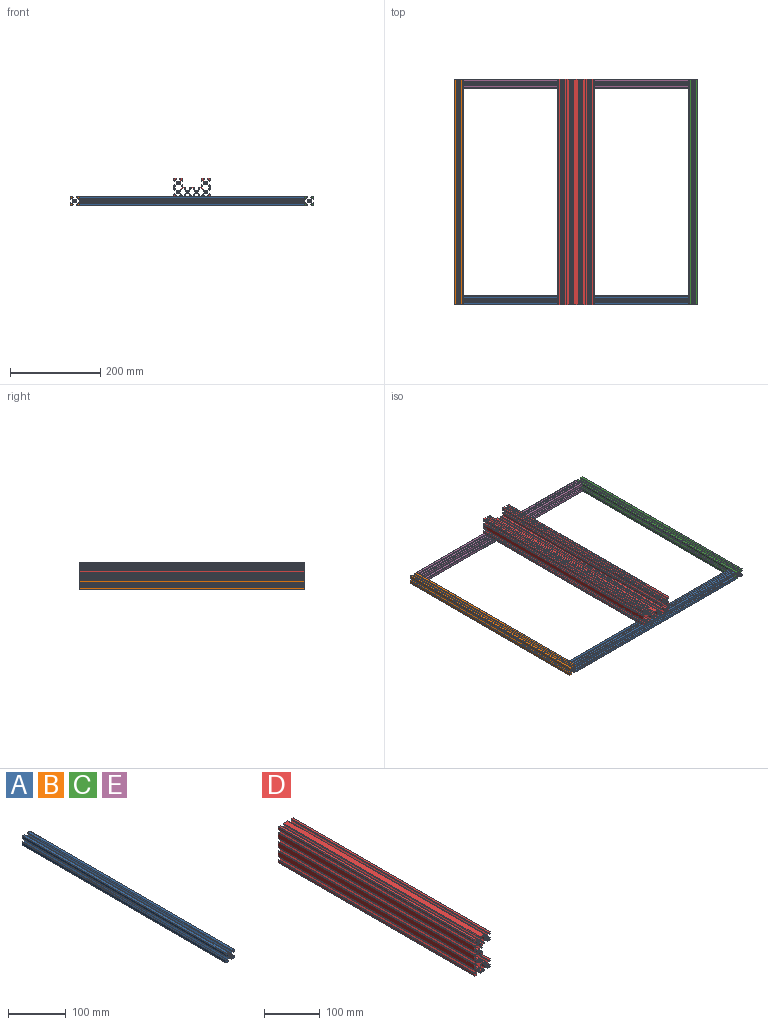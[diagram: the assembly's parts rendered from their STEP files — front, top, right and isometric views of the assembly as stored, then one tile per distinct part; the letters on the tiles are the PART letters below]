
ASSEMBLY  parts=5 mates=4
PART A: 71 faces, bbox 20x500x20 mm
  f0: cylinder r=2.1mm len=500mm, axis (0,1,0), area 6597.3mm2, adj f69,f70
  f1: plane 500x0.21mm, normal (0.71,0,0.71), area 148.5mm2, adj f2,f68,f69,f70
  f2: plane 500x0.21mm, normal (0.71,0,-0.71), area 148.5mm2, adj f1,f3,f69,f70
  f3: plane 500x2.63mm, normal (1,0,0), area 1314.7mm2, adj f2,f4,f69,f70
  f4: plane 500x2.66mm, normal (0.71,0,-0.71), area 1881.4mm2, adj f3,f5,f69,f70
  f5: plane 500x1.64mm, normal (0,0,-1), area 819.7mm2, adj f4,f6,f69,f70
  f6: plane 500x2.38mm, normal (-1,0,0), area 1187.5mm2, adj f5,f7,f69,f70
  f7: plane 500x0.35mm, normal (0,0,-1), area 172.5mm2, adj f6,f8,f69,f70
  f8: plane 500x1.46mm, normal (0.71,0,-0.71), area 1028.8mm2, adj f7,f9,f69,f70
  f9: plane 500x4.92mm, normal (1,0,0), area 2460mm2, adj f8,f10,f69,f70
  f10: cylinder r=0.5mm len=500mm, axis (0,1,0), area 392.7mm2, adj f9,f11,f69,f70
  f11: plane 500x4.92mm, normal (0,0,1), area 2460mm2, adj f10,f12,f69,f70
  f12: plane 500x1.46mm, normal (-0.71,0,0.71), area 1028.8mm2, adj f11,f13,f69,f70
  f13: plane 500x0.35mm, normal (-1,0,0), area 172.5mm2, adj f12,f14,f69,f70
  f14: plane 500x2.38mm, normal (0,0,-1), area 1187.5mm2, adj f13,f15,f69,f70
  f15: plane 500x1.64mm, normal (-1,0,0), area 819.7mm2, adj f14,f16,f69,f70
  f16: plane 500x2.66mm, normal (-0.71,0,0.71), area 1881.4mm2, adj f15,f17,f69,f70
  f17: plane 500x2.63mm, normal (0,0,1), area 1314.7mm2, adj f16,f18,f69,f70
  f18: plane 500x0.21mm, normal (-0.71,0,0.71), area 148.5mm2, adj f17,f19,f69,f70
  f19: plane 500x0.21mm, normal (0.71,0,0.71), area 148.5mm2, adj f18,f20,f69,f70
  f20: plane 500x2.63mm, normal (0,0,1), area 1314.7mm2, adj f19,f21,f69,f70
  f21: plane 500x2.66mm, normal (0.71,0,0.71), area 1881.4mm2, adj f20,f22,f69,f70
  f22: plane 500x1.64mm, normal (1,0,0), area 819.7mm2, adj f21,f23,f69,f70
  f23: plane 500x2.38mm, normal (0,0,-1), area 1187.5mm2, adj f22,f24,f69,f70
  f24: plane 500x0.35mm, normal (1,0,0), area 172.5mm2, adj f23,f25,f69,f70
  f25: plane 500x1.46mm, normal (0.71,0,0.71), area 1028.8mm2, adj f24,f26,f69,f70
  f26: plane 500x4.92mm, normal (0,0,1), area 2460mm2, adj f25,f27,f69,f70
  f27: cylinder r=0.5mm len=500mm, axis (0,1,0), area 392.7mm2, adj f26,f28,f69,f70
  f28: plane 500x4.92mm, normal (-1,0,0), area 2460mm2, adj f27,f29,f69,f70
  f29: plane 500x1.46mm, normal (-0.71,0,-0.71), area 1028.8mm2, adj f28,f30,f69,f70
  f30: plane 500x0.35mm, normal (0,0,-1), area 172.5mm2, adj f29,f31,f69,f70
  f31: plane 500x2.38mm, normal (1,0,0), area 1187.5mm2, adj f30,f32,f69,f70
  f32: plane 500x1.64mm, normal (0,0,-1), area 819.7mm2, adj f31,f33,f69,f70
  f33: plane 500x2.66mm, normal (-0.71,0,-0.71), area 1881.4mm2, adj f32,f34,f69,f70
  f34: plane 500x2.63mm, normal (-1,0,0), area 1314.7mm2, adj f33,f35,f69,f70
  f35: plane 500x0.21mm, normal (-0.71,0,-0.71), area 148.5mm2, adj f34,f36,f69,f70
  f36: plane 500x0.21mm, normal (-0.71,0,0.71), area 148.5mm2, adj f35,f37,f69,f70
  f37: plane 500x2.63mm, normal (-1,0,0), area 1314.7mm2, adj f36,f38,f69,f70
  f38: plane 500x2.66mm, normal (-0.71,0,0.71), area 1881.4mm2, adj f37,f39,f69,f70
  f39: plane 500x1.64mm, normal (0,0,1), area 819.7mm2, adj f38,f40,f69,f70
  f40: plane 500x2.38mm, normal (1,0,0), area 1187.5mm2, adj f39,f41,f69,f70
  f41: plane 500x0.35mm, normal (0,0,1), area 172.5mm2, adj f40,f42,f69,f70
  f42: plane 500x1.46mm, normal (-0.71,0,0.71), area 1028.8mm2, adj f41,f43,f69,f70
  f43: plane 500x4.92mm, normal (-1,0,0), area 2460mm2, adj f42,f44,f69,f70
  f44: cylinder r=0.5mm len=500mm, axis (0,1,0), area 392.7mm2, adj f43,f45,f69,f70
  f45: plane 500x4.92mm, normal (0,0,-1), area 2460mm2, adj f44,f46,f69,f70
  f46: plane 500x1.46mm, normal (0.71,0,-0.71), area 1028.8mm2, adj f45,f47,f69,f70
  f47: plane 500x0.35mm, normal (1,0,0), area 172.5mm2, adj f46,f48,f69,f70
  f48: plane 500x2.38mm, normal (0,0,1), area 1187.5mm2, adj f47,f49,f69,f70
  f49: plane 500x1.64mm, normal (1,0,0), area 819.7mm2, adj f48,f50,f69,f70
  f50: plane 500x2.66mm, normal (0.71,0,-0.71), area 1881.4mm2, adj f49,f51,f69,f70
  f51: plane 500x2.63mm, normal (0,0,-1), area 1314.7mm2, adj f50,f52,f69,f70
  f52: plane 500x0.21mm, normal (0.71,0,-0.71), area 148.5mm2, adj f51,f53,f69,f70
  f53: plane 500x0.21mm, normal (-0.71,0,-0.71), area 148.5mm2, adj f52,f54,f69,f70
  f54: plane 500x2.63mm, normal (0,0,-1), area 1314.7mm2, adj f53,f55,f69,f70
  f55: plane 500x2.66mm, normal (-0.71,0,-0.71), area 1881.4mm2, adj f54,f56,f69,f70
  f56: plane 500x1.64mm, normal (-1,0,0), area 819.7mm2, adj f55,f57,f69,f70
  f57: plane 500x2.38mm, normal (0,0,1), area 1187.5mm2, adj f56,f58,f69,f70
  f58: plane 500x0.35mm, normal (-1,0,0), area 172.5mm2, adj f57,f59,f69,f70
  f59: plane 500x1.46mm, normal (-0.71,0,-0.71), area 1028.8mm2, adj f58,f60,f69,f70
  f60: plane 500x4.92mm, normal (0,0,-1), area 2460mm2, adj f59,f61,f69,f70
  f61: cylinder r=0.5mm len=500mm, axis (0,1,0), area 392.7mm2, adj f60,f62,f69,f70
  f62: plane 500x4.92mm, normal (1,0,0), area 2460mm2, adj f61,f63,f69,f70
  f63: plane 500x1.46mm, normal (0.71,0,0.71), area 1028.8mm2, adj f62,f64,f69,f70
  f64: plane 500x0.35mm, normal (0,0,1), area 172.5mm2, adj f63,f65,f69,f70
  f65: plane 500x2.38mm, normal (-1,0,0), area 1187.5mm2, adj f64,f66,f69,f70
  f66: plane 500x1.64mm, normal (0,0,1), area 819.7mm2, adj f65,f67,f69,f70
  f67: plane 500x2.66mm, normal (0.71,0,0.71), area 1881.4mm2, adj f66,f68,f69,f70
  f68: plane 500x2.63mm, normal (1,0,0), area 1314.7mm2, adj f1,f67,f69,f70
  f69: plane 20x20mm, normal (0,-1,0), area 171.4mm2, adj f0,f1,f2,f3,f4,f5,f6,f7
  f70: plane 20x20mm, normal (0,1,0), area 171.4mm2, adj f0,f1,f2,f3,f4,f5,f6,f7
PART B: same geometry as A
PART C: same geometry as A
PART D: 288 faces, bbox 40x500x80 mm
  f0: cylinder r=2.3mm len=500mm, axis (0,1,0), area 7225.7mm2, adj f286,f287
  f1: cylinder r=2.3mm len=500mm, axis (0,1,0), area 7225.7mm2, adj f286,f287
  f2: cylinder r=2.3mm len=500mm, axis (0,1,0), area 7225.7mm2, adj f286,f287
  f3: cylinder r=2.3mm len=500mm, axis (0,1,0), area 7225.7mm2, adj f286,f287
  f4: cylinder r=2.3mm len=500mm, axis (0,1,0), area 7225.7mm2, adj f286,f287
  f5: cylinder r=2.3mm len=500mm, axis (0,1,0), area 7225.7mm2, adj f286,f287
  f6: plane 500x0.21mm, normal (0.71,0,0.71), area 148.5mm2, adj f7,f280,f286,f287
  f7: plane 500x0.21mm, normal (0.71,0,-0.71), area 148.5mm2, adj f6,f8,f286,f287
  f8: plane 500x2.63mm, normal (1,0,0), area 1314.7mm2, adj f7,f9,f286,f287
  f9: plane 500x2.66mm, normal (0.71,0,-0.71), area 1881.4mm2, adj f8,f10,f286,f287
  f10: plane 500x1.64mm, normal (0,0,-1), area 819.7mm2, adj f9,f11,f286,f287
  f11: plane 500x2.11mm, normal (-1,0,0), area 1052.5mm2, adj f10,f12,f286,f287
  f12: plane 500x0.62mm, normal (0,0,-1), area 307.5mm2, adj f11,f13,f286,f287
  f13: plane 500x1.19mm, normal (0.71,0,-0.71), area 837.9mm2, adj f12,f14,f286,f287
  f14: plane 500x3.92mm, normal (1,0,0), area 1960mm2, adj f13,f15,f286,f287
  f15: cylinder r=1.5mm len=500mm, axis (0,1,0), area 1178.1mm2, adj f14,f16,f286,f287
  f16: plane 500x3.92mm, normal (0,0,1), area 1960mm2, adj f15,f17,f286,f287
  f17: plane 500x1.19mm, normal (-0.71,0,0.71), area 837.9mm2, adj f16,f18,f286,f287
  f18: plane 500x0.62mm, normal (-1,0,0), area 307.5mm2, adj f17,f19,f286,f287
  f19: plane 500x2.11mm, normal (0,0,-1), area 1052.5mm2, adj f18,f20,f286,f287
  f20: plane 500x1.64mm, normal (-1,0,0), area 819.7mm2, adj f19,f21,f286,f287
  f21: plane 500x2.66mm, normal (-0.71,0,0.71), area 1881.4mm2, adj f20,f22,f286,f287
  f22: plane 500x2.63mm, normal (0,0,1), area 1314.7mm2, adj f21,f23,f286,f287
  f23: plane 500x0.21mm, normal (-0.71,0,0.71), area 148.5mm2, adj f22,f24,f286,f287
  f24: plane 500x0.21mm, normal (0.71,0,0.71), area 148.5mm2, adj f23,f25,f286,f287
  f25: plane 500x2.63mm, normal (0,0,1), area 1314.7mm2, adj f24,f26,f286,f287
  f26: plane 500x2.66mm, normal (0.71,0,0.71), area 1881.4mm2, adj f25,f27,f286,f287
  f27: plane 500x1.64mm, normal (1,0,0), area 819.7mm2, adj f26,f28,f286,f287
  f28: plane 500x2.11mm, normal (0,0,-1), area 1052.5mm2, adj f27,f29,f286,f287
  f29: plane 500x0.62mm, normal (1,0,0), area 307.5mm2, adj f28,f30,f286,f287
  f30: plane 500x1.19mm, normal (0.71,0,0.71), area 837.9mm2, adj f29,f31,f286,f287
  f31: plane 500x10.84mm, normal (0,0,1), area 5420mm2, adj f30,f32,f286,f287
  f32: plane 500x1.19mm, normal (-0.71,0,0.71), area 837.9mm2, adj f31,f33,f286,f287
  f33: plane 500x0.62mm, normal (-1,0,0), area 307.5mm2, adj f32,f34,f286,f287
  f34: plane 500x2.11mm, normal (0,0,-1), area 1052.5mm2, adj f33,f35,f286,f287
  f35: plane 500x1.64mm, normal (-1,0,0), area 819.7mm2, adj f34,f36,f286,f287
  f36: plane 500x2.66mm, normal (-0.71,0,0.71), area 1881.4mm2, adj f35,f37,f286,f287
  f37: plane 500x2.63mm, normal (0,0,1), area 1314.7mm2, adj f36,f38,f286,f287
  f38: plane 500x0.21mm, normal (-0.71,0,0.71), area 148.5mm2, adj f37,f39,f286,f287
  f39: plane 500x0.21mm, normal (0.71,0,0.71), area 148.5mm2, adj f38,f40,f286,f287
  f40: plane 500x2.63mm, normal (0,0,1), area 1314.7mm2, adj f39,f41,f286,f287
  f41: plane 500x2.66mm, normal (0.71,0,0.71), area 1881.4mm2, adj f40,f42,f286,f287
  f42: plane 500x1.64mm, normal (1,0,0), area 819.7mm2, adj f41,f43,f286,f287
  f43: plane 500x2.11mm, normal (0,0,-1), area 1052.5mm2, adj f42,f44,f286,f287
  f44: plane 500x0.62mm, normal (1,0,0), area 307.5mm2, adj f43,f45,f286,f287
  f45: plane 500x1.19mm, normal (0.71,0,0.71), area 837.9mm2, adj f44,f46,f286,f287
  f46: plane 500x3.92mm, normal (0,0,1), area 1960mm2, adj f45,f47,f286,f287
  f47: cylinder r=1.5mm len=500mm, axis (0,1,0), area 1178.1mm2, adj f46,f48,f286,f287
  f48: plane 500x3.92mm, normal (-1,0,0), area 1960mm2, adj f47,f49,f286,f287
  f49: plane 500x1.19mm, normal (-0.71,0,-0.71), area 837.9mm2, adj f48,f50,f286,f287
  f50: plane 500x0.62mm, normal (0,0,-1), area 307.5mm2, adj f49,f51,f286,f287
  f51: plane 500x2.11mm, normal (1,0,0), area 1052.5mm2, adj f50,f52,f286,f287
  f52: plane 500x1.64mm, normal (0,0,-1), area 819.7mm2, adj f51,f53,f286,f287
  f53: plane 500x2.66mm, normal (-0.71,0,-0.71), area 1881.4mm2, adj f52,f54,f286,f287
  f54: plane 500x2.63mm, normal (-1,0,0), area 1314.7mm2, adj f53,f55,f286,f287
  f55: plane 500x0.21mm, normal (-0.71,0,-0.71), area 148.5mm2, adj f54,f56,f286,f287
  f56: plane 500x0.21mm, normal (-0.71,0,0.71), area 148.5mm2, adj f55,f57,f286,f287
  f57: plane 500x2.63mm, normal (-1,0,0), area 1314.7mm2, adj f56,f58,f286,f287
  f58: plane 500x2.66mm, normal (-0.71,0,0.71), area 1881.4mm2, adj f57,f59,f286,f287
  f59: plane 500x1.64mm, normal (0,0,1), area 819.7mm2, adj f58,f60,f286,f287
  f60: plane 500x2.11mm, normal (1,0,0), area 1052.5mm2, adj f59,f61,f286,f287
  f61: plane 500x0.62mm, normal (0,0,1), area 307.5mm2, adj f60,f62,f286,f287
  f62: plane 500x1.19mm, normal (-0.71,0,0.71), area 837.9mm2, adj f61,f63,f286,f287
  f63: plane 500x10.84mm, normal (-1,0,0), area 5420mm2, adj f62,f64,f286,f287
  f64: plane 500x1.19mm, normal (-0.71,0,-0.71), area 837.9mm2, adj f63,f65,f286,f287
  f65: plane 500x0.62mm, normal (0,0,-1), area 307.5mm2, adj f64,f66,f286,f287
  f66: plane 500x2.11mm, normal (1,0,0), area 1052.5mm2, adj f65,f67,f286,f287
  f67: plane 500x1.64mm, normal (0,0,-1), area 819.7mm2, adj f66,f68,f286,f287
  f68: plane 500x2.66mm, normal (-0.71,0,-0.71), area 1881.4mm2, adj f67,f69,f286,f287
  f69: plane 500x2.63mm, normal (-1,0,0), area 1314.7mm2, adj f68,f70,f286,f287
  f70: plane 500x0.21mm, normal (-0.71,0,-0.71), area 148.5mm2, adj f69,f71,f286,f287
  f71: plane 500x0.21mm, normal (-0.71,0,0.71), area 148.5mm2, adj f70,f72,f286,f287
  f72: plane 500x2.63mm, normal (-1,0,0), area 1314.7mm2, adj f71,f73,f286,f287
  f73: plane 500x2.66mm, normal (-0.71,0,0.71), area 1881.4mm2, adj f72,f74,f286,f287
  f74: plane 500x1.64mm, normal (0,0,1), area 819.7mm2, adj f73,f75,f286,f287
  f75: plane 500x2.11mm, normal (1,0,0), area 1052.5mm2, adj f74,f76,f286,f287
  f76: plane 500x0.62mm, normal (0,0,1), area 307.5mm2, adj f75,f77,f286,f287
  f77: plane 500x1.19mm, normal (-0.71,0,0.71), area 837.9mm2, adj f76,f78,f286,f287
  f78: plane 500x10.84mm, normal (-1,0,0), area 5420mm2, adj f77,f79,f286,f287
  f79: plane 500x1.19mm, normal (-0.71,0,-0.71), area 837.9mm2, adj f78,f80,f286,f287
  f80: plane 500x0.62mm, normal (0,0,-1), area 307.5mm2, adj f79,f81,f286,f287
  f81: plane 500x2.11mm, normal (1,0,0), area 1052.5mm2, adj f80,f82,f286,f287
  f82: plane 500x1.64mm, normal (0,0,-1), area 819.7mm2, adj f81,f83,f286,f287
  f83: plane 500x2.66mm, normal (-0.71,0,-0.71), area 1881.4mm2, adj f82,f84,f286,f287
  f84: plane 500x2.63mm, normal (-1,0,0), area 1314.7mm2, adj f83,f85,f286,f287
  f85: plane 500x0.21mm, normal (-0.71,0,-0.71), area 148.5mm2, adj f84,f86,f286,f287
  f86: plane 500x0.21mm, normal (-0.71,0,0.71), area 148.5mm2, adj f85,f87,f286,f287
  f87: plane 500x2.63mm, normal (-1,0,0), area 1314.7mm2, adj f86,f88,f286,f287
  f88: plane 500x2.66mm, normal (-0.71,0,0.71), area 1881.4mm2, adj f87,f89,f286,f287
  f89: plane 500x1.64mm, normal (0,0,1), area 819.7mm2, adj f88,f90,f286,f287
  f90: plane 500x2.11mm, normal (1,0,0), area 1052.5mm2, adj f89,f91,f286,f287
  f91: plane 500x0.62mm, normal (0,0,1), area 307.5mm2, adj f90,f92,f286,f287
  f92: plane 500x1.19mm, normal (-0.71,0,0.71), area 837.9mm2, adj f91,f93,f286,f287
  f93: plane 500x10.84mm, normal (-1,0,0), area 5420mm2, adj f92,f94,f286,f287
  f94: plane 500x1.19mm, normal (-0.71,0,-0.71), area 837.9mm2, adj f93,f95,f286,f287
  f95: plane 500x0.62mm, normal (0,0,-1), area 307.5mm2, adj f94,f96,f286,f287
  f96: plane 500x2.11mm, normal (1,0,0), area 1052.5mm2, adj f95,f97,f286,f287
  f97: plane 500x1.64mm, normal (0,0,-1), area 819.7mm2, adj f96,f98,f286,f287
  f98: plane 500x2.66mm, normal (-0.71,0,-0.71), area 1881.4mm2, adj f97,f99,f286,f287
  f99: plane 500x2.63mm, normal (-1,0,0), area 1314.7mm2, adj f98,f100,f286,f287
  f100: plane 500x0.21mm, normal (-0.71,0,-0.71), area 148.5mm2, adj f99,f101,f286,f287
  f101: plane 500x0.21mm, normal (-0.71,0,0.71), area 148.5mm2, adj f100,f102,f286,f287
  f102: plane 500x2.63mm, normal (-1,0,0), area 1314.7mm2, adj f101,f103,f286,f287
  f103: plane 500x2.66mm, normal (-0.71,0,0.71), area 1881.4mm2, adj f102,f104,f286,f287
  f104: plane 500x1.64mm, normal (0,0,1), area 819.7mm2, adj f103,f105,f286,f287
  f105: plane 500x2.11mm, normal (1,0,0), area 1052.5mm2, adj f104,f106,f286,f287
  f106: plane 500x0.62mm, normal (0,0,1), area 307.5mm2, adj f105,f107,f286,f287
  f107: plane 500x1.19mm, normal (-0.71,0,0.71), area 837.9mm2, adj f106,f108,f286,f287
  f108: plane 500x3.92mm, normal (-1,0,0), area 1960mm2, adj f107,f109,f286,f287
  f109: cylinder r=1.5mm len=500mm, axis (0,1,0), area 1178.1mm2, adj f108,f110,f286,f287
  f110: plane 500x3.92mm, normal (0,0,-1), area 1960mm2, adj f109,f111,f286,f287
  f111: plane 500x1.19mm, normal (0.71,0,-0.71), area 837.9mm2, adj f110,f112,f286,f287
  f112: plane 500x0.62mm, normal (1,0,0), area 307.5mm2, adj f111,f113,f286,f287
  f113: plane 500x2.11mm, normal (0,0,1), area 1052.5mm2, adj f112,f114,f286,f287
  f114: plane 500x1.64mm, normal (1,0,0), area 819.7mm2, adj f113,f115,f286,f287
  f115: plane 500x2.66mm, normal (0.71,0,-0.71), area 1881.4mm2, adj f114,f116,f286,f287
  f116: plane 500x2.63mm, normal (0,0,-1), area 1314.7mm2, adj f115,f117,f286,f287
  f117: plane 500x0.21mm, normal (0.71,0,-0.71), area 148.5mm2, adj f116,f118,f286,f287
  f118: plane 500x0.21mm, normal (-0.71,0,-0.71), area 148.5mm2, adj f117,f119,f286,f287
  f119: plane 500x2.63mm, normal (0,0,-1), area 1314.7mm2, adj f118,f120,f286,f287
  f120: plane 500x2.66mm, normal (-0.71,0,-0.71), area 1881.4mm2, adj f119,f121,f286,f287
  f121: plane 500x1.64mm, normal (-1,0,0), area 819.7mm2, adj f120,f122,f286,f287
  f122: plane 500x2.11mm, normal (0,0,1), area 1052.5mm2, adj f121,f123,f286,f287
  f123: plane 500x0.62mm, normal (-1,0,0), area 307.5mm2, adj f122,f124,f286,f287
  f124: plane 500x1.19mm, normal (-0.71,0,-0.71), area 837.9mm2, adj f123,f125,f286,f287
  f125: plane 500x10.84mm, normal (0,0,-1), area 5420mm2, adj f124,f126,f286,f287
  f126: plane 500x1.19mm, normal (0.71,0,-0.71), area 837.9mm2, adj f125,f127,f286,f287
  f127: plane 500x0.62mm, normal (1,0,0), area 307.5mm2, adj f126,f128,f286,f287
  f128: plane 500x2.11mm, normal (0,0,1), area 1052.5mm2, adj f127,f129,f286,f287
  f129: plane 500x1.64mm, normal (1,0,0), area 819.7mm2, adj f128,f130,f286,f287
  f130: plane 500x2.66mm, normal (0.71,0,-0.71), area 1881.4mm2, adj f129,f131,f286,f287
  f131: plane 500x2.63mm, normal (0,0,-1), area 1314.7mm2, adj f130,f132,f286,f287
  f132: plane 500x0.21mm, normal (0.71,0,-0.71), area 148.5mm2, adj f131,f133,f286,f287
  f133: plane 500x0.21mm, normal (-0.71,0,-0.71), area 148.5mm2, adj f132,f134,f286,f287
  f134: plane 500x2.63mm, normal (0,0,-1), area 1314.7mm2, adj f133,f135,f286,f287
  f135: plane 500x2.66mm, normal (-0.71,0,-0.71), area 1881.4mm2, adj f134,f136,f286,f287
  f136: plane 500x1.64mm, normal (-1,0,0), area 819.7mm2, adj f135,f137,f286,f287
  f137: plane 500x2.11mm, normal (0,0,1), area 1052.5mm2, adj f136,f138,f286,f287
  f138: plane 500x0.62mm, normal (-1,0,0), area 307.5mm2, adj f137,f139,f286,f287
  f139: plane 500x1.19mm, normal (-0.71,0,-0.71), area 837.9mm2, adj f138,f140,f286,f287
  f140: plane 500x3.92mm, normal (0,0,-1), area 1960mm2, adj f139,f141,f286,f287
  f141: cylinder r=1.5mm len=500mm, axis (0,1,0), area 1178.1mm2, adj f140,f142,f286,f287
  f142: plane 500x3.92mm, normal (1,0,0), area 1960mm2, adj f141,f143,f286,f287
  f143: plane 500x1.19mm, normal (0.71,0,0.71), area 837.9mm2, adj f142,f144,f286,f287
  f144: plane 500x0.62mm, normal (0,0,1), area 307.5mm2, adj f143,f145,f286,f287
  f145: plane 500x2.11mm, normal (-1,0,0), area 1052.5mm2, adj f144,f146,f286,f287
  f146: plane 500x1.64mm, normal (0,0,1), area 819.7mm2, adj f145,f147,f286,f287
  f147: plane 500x2.66mm, normal (0.71,0,0.71), area 1881.4mm2, adj f146,f148,f286,f287
  f148: plane 500x2.63mm, normal (1,0,0), area 1314.7mm2, adj f147,f149,f286,f287
  f149: plane 500x0.21mm, normal (0.71,0,0.71), area 148.5mm2, adj f148,f150,f286,f287
  f150: plane 500x0.21mm, normal (0.71,0,-0.71), area 148.5mm2, adj f149,f151,f286,f287
  f151: plane 500x2.63mm, normal (1,0,0), area 1314.7mm2, adj f150,f152,f286,f287
  f152: plane 500x2.66mm, normal (0.71,0,-0.71), area 1881.4mm2, adj f151,f153,f286,f287
  f153: plane 500x1.64mm, normal (0,0,-1), area 819.7mm2, adj f152,f154,f286,f287
  f154: plane 500x2.11mm, normal (-1,0,0), area 1052.5mm2, adj f153,f155,f286,f287
  f155: plane 500x0.62mm, normal (0,0,-1), area 307.5mm2, adj f154,f156,f286,f287
  f156: plane 500x1.19mm, normal (0.71,0,-0.71), area 837.9mm2, adj f155,f157,f286,f287
  f157: plane 500x3.92mm, normal (1,0,0), area 1960mm2, adj f156,f158,f286,f287
  f158: cylinder r=1.5mm len=500mm, axis (0,1,0), area 1178.1mm2, adj f157,f159,f286,f287
  f159: plane 500x3.92mm, normal (0,0,1), area 1960mm2, adj f158,f160,f286,f287
  f160: plane 500x1.19mm, normal (-0.71,0,0.71), area 837.9mm2, adj f159,f161,f286,f287
  f161: plane 500x0.62mm, normal (-1,0,0), area 307.5mm2, adj f160,f162,f286,f287
  f162: plane 500x2.11mm, normal (0,0,-1), area 1052.5mm2, adj f161,f163,f286,f287
  f163: plane 500x1.64mm, normal (-1,0,0), area 819.7mm2, adj f162,f164,f286,f287
  f164: plane 500x2.66mm, normal (-0.71,0,0.71), area 1881.4mm2, adj f163,f165,f286,f287
  f165: plane 500x2.63mm, normal (0,0,1), area 1314.7mm2, adj f164,f166,f286,f287
  f166: plane 500x0.21mm, normal (-0.71,0,0.71), area 148.5mm2, adj f165,f167,f286,f287
  f167: plane 500x0.21mm, normal (0.71,0,0.71), area 148.5mm2, adj f166,f168,f286,f287
  f168: plane 500x2.63mm, normal (0,0,1), area 1314.7mm2, adj f167,f169,f286,f287
  f169: plane 500x2.66mm, normal (0.71,0,0.71), area 1881.4mm2, adj f168,f170,f286,f287
  f170: plane 500x1.64mm, normal (1,0,0), area 819.7mm2, adj f169,f171,f286,f287
  f171: plane 500x2.11mm, normal (0,0,-1), area 1052.5mm2, adj f170,f172,f286,f287
  f172: plane 500x0.62mm, normal (1,0,0), area 307.5mm2, adj f171,f173,f286,f287
  f173: plane 500x1.19mm, normal (0.71,0,0.71), area 837.9mm2, adj f172,f174,f286,f287
  f174: plane 500x5.42mm, normal (0,0,1), area 2710mm2, adj f173,f175,f286,f287
  f175: plane 500x5.42mm, normal (1,0,0), area 2710mm2, adj f174,f176,f286,f287
  f176: plane 500x1.19mm, normal (0.71,0,0.71), area 837.9mm2, adj f175,f177,f286,f287
  f177: plane 500x0.62mm, normal (0,0,1), area 307.5mm2, adj f176,f178,f286,f287
  f178: plane 500x2.11mm, normal (-1,0,0), area 1052.5mm2, adj f177,f179,f286,f287
  f179: plane 500x1.64mm, normal (0,0,1), area 819.7mm2, adj f178,f180,f286,f287
  f180: plane 500x2.66mm, normal (0.71,0,0.71), area 1881.4mm2, adj f179,f181,f286,f287
  f181: plane 500x2.63mm, normal (1,0,0), area 1314.7mm2, adj f180,f182,f286,f287
  f182: plane 500x0.21mm, normal (0.71,0,0.71), area 148.5mm2, adj f181,f183,f286,f287
  f183: plane 500x0.21mm, normal (0.71,0,-0.71), area 148.5mm2, adj f182,f184,f286,f287
  f184: plane 500x2.63mm, normal (1,0,0), area 1314.7mm2, adj f183,f185,f286,f287
  f185: plane 500x2.66mm, normal (0.71,0,-0.71), area 1881.4mm2, adj f184,f186,f286,f287
  f186: plane 500x1.64mm, normal (0,0,-1), area 819.7mm2, adj f185,f187,f286,f287
  f187: plane 500x2.11mm, normal (-1,0,0), area 1052.5mm2, adj f186,f188,f286,f287
  f188: plane 500x0.62mm, normal (0,0,-1), area 307.5mm2, adj f187,f189,f286,f287
  f189: plane 500x1.19mm, normal (0.71,0,-0.71), area 837.9mm2, adj f188,f190,f286,f287
  f190: plane 500x10.84mm, normal (1,0,0), area 5420mm2, adj f189,f191,f286,f287
  f191: plane 500x1.19mm, normal (0.71,0,0.71), area 837.9mm2, adj f190,f192,f286,f287
  f192: plane 500x0.62mm, normal (0,0,1), area 307.5mm2, adj f191,f193,f286,f287
  f193: plane 500x2.11mm, normal (-1,0,0), area 1052.5mm2, adj f192,f194,f286,f287
  f194: plane 500x1.64mm, normal (0,0,1), area 819.7mm2, adj f193,f195,f286,f287
  f195: plane 500x2.66mm, normal (0.71,0,0.71), area 1881.4mm2, adj f194,f196,f286,f287
  f196: plane 500x2.63mm, normal (1,0,0), area 1314.7mm2, adj f195,f197,f286,f287
  f197: plane 500x0.21mm, normal (0.71,0,0.71), area 148.5mm2, adj f196,f198,f286,f287
  f198: plane 500x0.21mm, normal (0.71,0,-0.71), area 148.5mm2, adj f197,f199,f286,f287
  f199: plane 500x2.63mm, normal (1,0,0), area 1314.7mm2, adj f198,f200,f286,f287
  f200: plane 500x2.66mm, normal (0.71,0,-0.71), area 1881.4mm2, adj f199,f201,f286,f287
  f201: plane 500x1.64mm, normal (0,0,-1), area 819.7mm2, adj f200,f202,f286,f287
  f202: plane 500x2.11mm, normal (-1,0,0), area 1052.5mm2, adj f201,f203,f286,f287
  f203: plane 500x0.62mm, normal (0,0,-1), area 307.5mm2, adj f202,f204,f286,f287
  f204: plane 500x1.19mm, normal (0.71,0,-0.71), area 837.9mm2, adj f203,f205,f286,f287
  f205: plane 500x5.42mm, normal (1,0,0), area 2710mm2, adj f204,f206,f286,f287
  f206: plane 500x5.42mm, normal (0,0,-1), area 2710mm2, adj f205,f207,f286,f287
  f207: plane 500x1.19mm, normal (0.71,0,-0.71), area 837.9mm2, adj f206,f208,f286,f287
  f208: plane 500x0.62mm, normal (1,0,0), area 307.5mm2, adj f207,f209,f286,f287
  f209: plane 500x2.11mm, normal (0,0,1), area 1052.5mm2, adj f208,f210,f286,f287
  f210: plane 500x1.64mm, normal (1,0,0), area 819.7mm2, adj f209,f211,f286,f287
  f211: plane 500x2.66mm, normal (0.71,0,-0.71), area 1881.4mm2, adj f210,f212,f286,f287
  f212: plane 500x2.63mm, normal (0,0,-1), area 1314.7mm2, adj f211,f213,f286,f287
  f213: plane 500x0.21mm, normal (0.71,0,-0.71), area 148.5mm2, adj f212,f214,f286,f287
  f214: plane 500x0.21mm, normal (-0.71,0,-0.71), area 148.5mm2, adj f213,f215,f286,f287
  f215: plane 500x2.63mm, normal (0,0,-1), area 1314.7mm2, adj f214,f216,f286,f287
  f216: plane 500x2.66mm, normal (-0.71,0,-0.71), area 1881.4mm2, adj f215,f217,f286,f287
  f217: plane 500x1.64mm, normal (-1,0,0), area 819.7mm2, adj f216,f218,f286,f287
  f218: plane 500x2.11mm, normal (0,0,1), area 1052.5mm2, adj f217,f219,f286,f287
  f219: plane 500x0.62mm, normal (-1,0,0), area 307.5mm2, adj f218,f220,f286,f287
  f220: plane 500x1.19mm, normal (-0.71,0,-0.71), area 837.9mm2, adj f219,f221,f286,f287
  f221: plane 500x3.92mm, normal (0,0,-1), area 1960mm2, adj f220,f222,f286,f287
  f222: cylinder r=1.5mm len=500mm, axis (0,1,0), area 1178.1mm2, adj f221,f223,f286,f287
  f223: plane 500x3.92mm, normal (1,0,0), area 1960mm2, adj f222,f224,f286,f287
  f224: plane 500x1.19mm, normal (0.71,0,0.71), area 837.9mm2, adj f223,f225,f286,f287
  f225: plane 500x0.62mm, normal (0,0,1), area 307.5mm2, adj f224,f226,f286,f287
  f226: plane 500x2.11mm, normal (-1,0,0), area 1052.5mm2, adj f225,f227,f286,f287
  f227: plane 500x1.64mm, normal (0,0,1), area 819.7mm2, adj f226,f228,f286,f287
  f228: plane 500x2.66mm, normal (0.71,0,0.71), area 1881.4mm2, adj f227,f280,f286,f287
  f229: plane 500x1.96mm, normal (0,0,1), area 980.3mm2, adj f230,f281,f286,f287
  f230: plane 500x5.4mm, normal (1,0,0), area 2700mm2, adj f229,f231,f286,f287
  f231: plane 500x1.96mm, normal (0,0,-1), area 980.3mm2, adj f230,f232,f286,f287
  f232: plane 500x3.4mm, normal (0.71,0,-0.71), area 2404.2mm2, adj f231,f233,f286,f287
  f233: plane 500x5.68mm, normal (0,0,-1), area 2839.3mm2, adj f232,f234,f286,f287
  f234: plane 500x3.4mm, normal (-0.71,0,-0.71), area 2404.2mm2, adj f233,f235,f286,f287
  f235: plane 500x1.96mm, normal (0,0,-1), area 980.3mm2, adj f234,f236,f286,f287
  f236: plane 500x5.4mm, normal (-1,0,0), area 2700mm2, adj f235,f237,f286,f287
  f237: plane 500x1.96mm, normal (0,0,1), area 980.3mm2, adj f236,f238,f286,f287
  f238: plane 500x3.4mm, normal (-0.71,0,0.71), area 2404.2mm2, adj f237,f239,f286,f287
  f239: plane 500x5.68mm, normal (0,0,1), area 2839.3mm2, adj f238,f281,f286,f287
  f240: plane 500x1.96mm, normal (0,0,1), area 980.3mm2, adj f241,f282,f286,f287
  f241: plane 500x5.4mm, normal (1,0,0), area 2700mm2, adj f240,f242,f286,f287
  f242: plane 500x1.96mm, normal (0,0,-1), area 980.3mm2, adj f241,f243,f286,f287
  f243: plane 500x3.4mm, normal (0.71,0,-0.71), area 2404.2mm2, adj f242,f244,f286,f287
  f244: plane 500x5.68mm, normal (0,0,-1), area 2839.3mm2, adj f243,f245,f286,f287
  f245: plane 500x5.36mm, normal (-0.71,0,-0.71), area 3790.6mm2, adj f244,f246,f286,f287
  f246: plane 500x3.44mm, normal (-1,0,0), area 1719.7mm2, adj f245,f247,f286,f287
  f247: plane 500x1.96mm, normal (0,0,1), area 980.3mm2, adj f246,f248,f286,f287
  f248: plane 500x3.4mm, normal (-0.71,0,0.71), area 2404.2mm2, adj f247,f249,f286,f287
  f249: plane 500x5.68mm, normal (0,0,1), area 2839.3mm2, adj f248,f282,f286,f287
  f250: plane 500x1.96mm, normal (-1,0,0), area 980.3mm2, adj f251,f283,f286,f287
  f251: plane 500x5.4mm, normal (0,0,1), area 2700mm2, adj f250,f252,f286,f287
  f252: plane 500x1.96mm, normal (1,0,0), area 980.3mm2, adj f251,f253,f286,f287
  f253: plane 500x3.4mm, normal (0.71,0,0.71), area 2404.2mm2, adj f252,f254,f286,f287
  f254: plane 500x5.68mm, normal (1,0,0), area 2839.3mm2, adj f253,f255,f286,f287
  f255: plane 500x5.36mm, normal (0.71,0,-0.71), area 3790.6mm2, adj f254,f256,f286,f287
  f256: plane 500x3.44mm, normal (0,0,-1), area 1719.7mm2, adj f255,f257,f286,f287
  f257: plane 500x1.96mm, normal (-1,0,0), area 980.3mm2, adj f256,f258,f286,f287
  f258: plane 500x3.4mm, normal (-0.71,0,-0.71), area 2404.2mm2, adj f257,f259,f286,f287
  f259: plane 500x5.68mm, normal (-1,0,0), area 2839.3mm2, adj f258,f283,f286,f287
  f260: plane 500x1.96mm, normal (0,0,1), area 980.3mm2, adj f261,f284,f286,f287
  f261: plane 500x5.4mm, normal (1,0,0), area 2700mm2, adj f260,f262,f286,f287
  f262: plane 500x1.96mm, normal (0,0,-1), area 980.3mm2, adj f261,f263,f286,f287
  f263: plane 500x3.4mm, normal (0.71,0,-0.71), area 2404.2mm2, adj f262,f264,f286,f287
  f264: plane 500x5.68mm, normal (0,0,-1), area 2839.3mm2, adj f263,f265,f286,f287
  f265: plane 500x3.4mm, normal (-0.71,0,-0.71), area 2404.2mm2, adj f264,f266,f286,f287
  f266: plane 500x1.96mm, normal (0,0,-1), area 980.3mm2, adj f265,f267,f286,f287
  f267: plane 500x3.44mm, normal (-1,0,0), area 1719.7mm2, adj f266,f268,f286,f287
  f268: plane 500x5.36mm, normal (-0.71,0,0.71), area 3790.6mm2, adj f267,f269,f286,f287
  f269: plane 500x5.68mm, normal (0,0,1), area 2839.3mm2, adj f268,f284,f286,f287
  f270: plane 500x1.96mm, normal (1,0,0), area 980.3mm2, adj f271,f285,f286,f287
  f271: plane 500x5.4mm, normal (0,0,-1), area 2700mm2, adj f270,f272,f286,f287
  f272: plane 500x1.96mm, normal (-1,0,0), area 980.3mm2, adj f271,f273,f286,f287
  f273: plane 500x3.4mm, normal (-0.71,0,-0.71), area 2404.2mm2, adj f272,f274,f286,f287
  f274: plane 500x5.68mm, normal (-1,0,0), area 2839.3mm2, adj f273,f275,f286,f287
  f275: plane 500x3.4mm, normal (-0.71,0,0.71), area 2404.2mm2, adj f274,f276,f286,f287
  f276: plane 500x1.96mm, normal (-1,0,0), area 980.3mm2, adj f275,f277,f286,f287
  f277: plane 500x3.44mm, normal (0,0,1), area 1719.7mm2, adj f276,f278,f286,f287
  f278: plane 500x5.36mm, normal (0.71,0,0.71), area 3790.6mm2, adj f277,f279,f286,f287
  f279: plane 500x5.68mm, normal (1,0,0), area 2839.3mm2, adj f278,f285,f286,f287
  f280: plane 500x2.63mm, normal (1,0,0), area 1314.7mm2, adj f6,f228,f286,f287
  f281: plane 500x3.4mm, normal (0.71,0,0.71), area 2404.2mm2, adj f229,f239,f286,f287
  f282: plane 500x3.4mm, normal (0.71,0,0.71), area 2404.2mm2, adj f240,f249,f286,f287
  f283: plane 500x3.4mm, normal (-0.71,0,0.71), area 2404.2mm2, adj f250,f259,f286,f287
  f284: plane 500x3.4mm, normal (0.71,0,0.71), area 2404.2mm2, adj f260,f269,f286,f287
  f285: plane 500x3.4mm, normal (0.71,0,-0.71), area 2404.2mm2, adj f270,f279,f286,f287
  f286: plane 80x40mm, normal (0,-1,0), area 799.1mm2, adj f0,f1,f2,f3,f4,f5,f6,f7
  f287: plane 80x40mm, normal (0,1,0), area 799.1mm2, adj f0,f1,f2,f3,f4,f5,f6,f7
PART E: same geometry as A
PLACE A rot(axis=(-0.58,0.58,0.58),120deg) t=(-54.49,-593.53,-121.41)mm
PLACE B t=(-64.49,-103.53,-121.45)mm
PLACE C rot(axis=(0,0,1),180deg) t=(455.51,-603.53,-121.45)mm
PLACE D rot(axis=(0,-1,0),90deg) t=(195.51,-103.49,-91.41)mm
PLACE E rot(axis=(-0.58,0.58,0.58),120deg) t=(-54.49,-113.53,-121.49)mm
MATE fastened A.f0 <-> C.f9  axis (1,0,0) through (445.51,-593.53,-121.41)mm
MATE fastened E.f0 <-> B.f62  axis (-1,0,0) through (-54.49,-113.53,-121.49)mm
MATE fastened E.f0 <-> C.f62  axis (1,0,0) through (445.51,-113.53,-121.49)mm
MATE fastened A.f28 <-> D.f78  axis (0,0,1) through (195.51,-586.49,-111.41)mm
